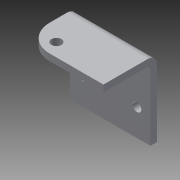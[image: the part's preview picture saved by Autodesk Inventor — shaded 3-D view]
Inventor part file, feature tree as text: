
AUTODESK INVENTOR PART (.ipt)
format: ipt  version: 2014 (Build 180170000, 170)  size: 122,880 bytes
history: native  units: in
note: dims shown in document units (in); Inventor stores cm internally (conversion verified against a paired STEP export)
features: sheet_metal_op x4, sketch x3, other x3
ambient origin geometry x8: Origin, YZ Plane, XZ Plane, XY Plane, X Axis, Y Axis, Z Axis, Center Point
bodies: Solid1 (feature_tree)
feature tree (10):
  sheet_metal_op  "Face1"
  sheet_metal_op  "Flange1"
  sketch  "Sketch1"  dims[d0=1.5in]
  other  "Plate1"
  sketch  "Sketch2"  dims[d1=1.25in]
  other  "Plate2"
  sheet_metal_op  "Bend1"
  sheet_metal_op  "Corner1"
  sketch  "Sketch4"  dims[d2=0.163in d3=0.25in d4=0.7874in d6=1.0in d7=0.3937in d9=1.0in d11=0.125in d12=0.125in d13=0.0625in d14=0.25in d15=0.125in d16=1.0in d17=90.0deg d18=0.05in d19=0.5in d20=0.125in d21=0.125in d22=0.5in d28=0.187in d29=0.25in d31=0.125in d32=0.0in d34=0.375in d35=0.5in]
  other  "Cut2"
